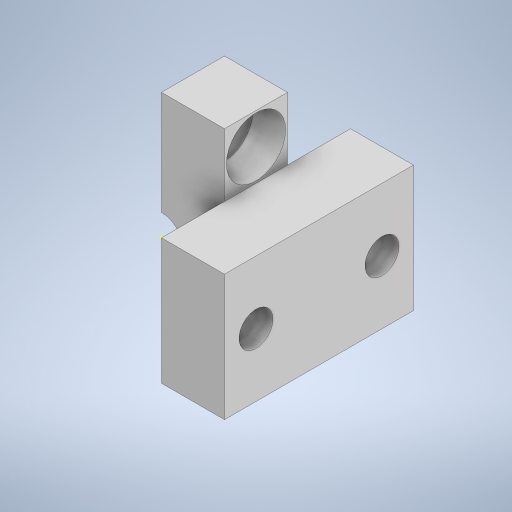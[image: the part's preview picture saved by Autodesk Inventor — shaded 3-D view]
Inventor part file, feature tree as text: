
AUTODESK INVENTOR PART (.ipt)
format: ipt  version: 2023 (Build 270158000, 158)  size: 343,552 bytes
history: native  units: mm
features: sketch x10, extrude x9, plane x1
ambient origin geometry x8: Origin, YZ Plane, XZ Plane, XY Plane, X Axis, Y Axis, Z Axis, Center Point
bodies: Solid1 (feature_tree)
feature tree (20):
  extrude  "Extrusion1"  Depth=20.0mm
  plane  "Work Plane1"
  extrude  "Extrusion2"  Depth=5.0mm
  extrude  "Extrusion3"  Depth=3.5mm
  extrude  "Extrusion4"  Depth=2.5mm
  extrude  "Extrusion5"  Depth=2.5mm
  sketch  "Sketch6"  dims[d21=2.5mm d22=2.7mm]
  extrude  "Extrusion6"  Depth=2.5mm
  extrude  "Extrusion7"  Depth=25.0mm TaperAngle=0.0deg
  extrude  "Extrusion8"  Depth=4.0mm
  extrude  "Extrusion9"  Depth=5.0mm
  sketch  "Sketch1"  dims[d0=20.0mm d1=20.0mm]
  sketch  "Sketch2"  dims[d10=5.0mm d11=0.0mm d12=5.0mm]
  sketch  "Sketch3"  dims[d13=2.0mm d14=0.0mm d15=3.5mm]
  sketch  "Sketch4"  dims[d16=8.0mm d17=0.0mm d18=2.5mm]
  sketch  "Sketch5"  dims[d19=2.5mm d20=2.5mm]
  sketch  "Sketch7"  dims[d23=2.7mm d24=25.0mm d25=0.0mm]
  sketch  "Sketch8"  dims[d26=4.0mm d27=4.0mm]
  sketch  "Sketch9"  dims[d28=4.0mm d29=0.0mm d30=5.0mm]
  sketch  "Sketch10"  dims[d31=5.0mm d32=5.0mm d33=5.0mm d34=10.0mm d35=0.0mm d36=5.0mm d37=5.0mm d38=5.0mm d39=2.7mm d40=2.7mm d41=5.0mm d42=5.0mm d43=5.0mm d44=5.0mm d45=2.5mm d46=2.5mm d47=5.0mm d48=0.0mm d49=4.0mm d50=4.0mm d51=2.0mm d52=0.0mm d53=4.7mm d54=4.7mm d55=2.6mm d56=0.0mm]
